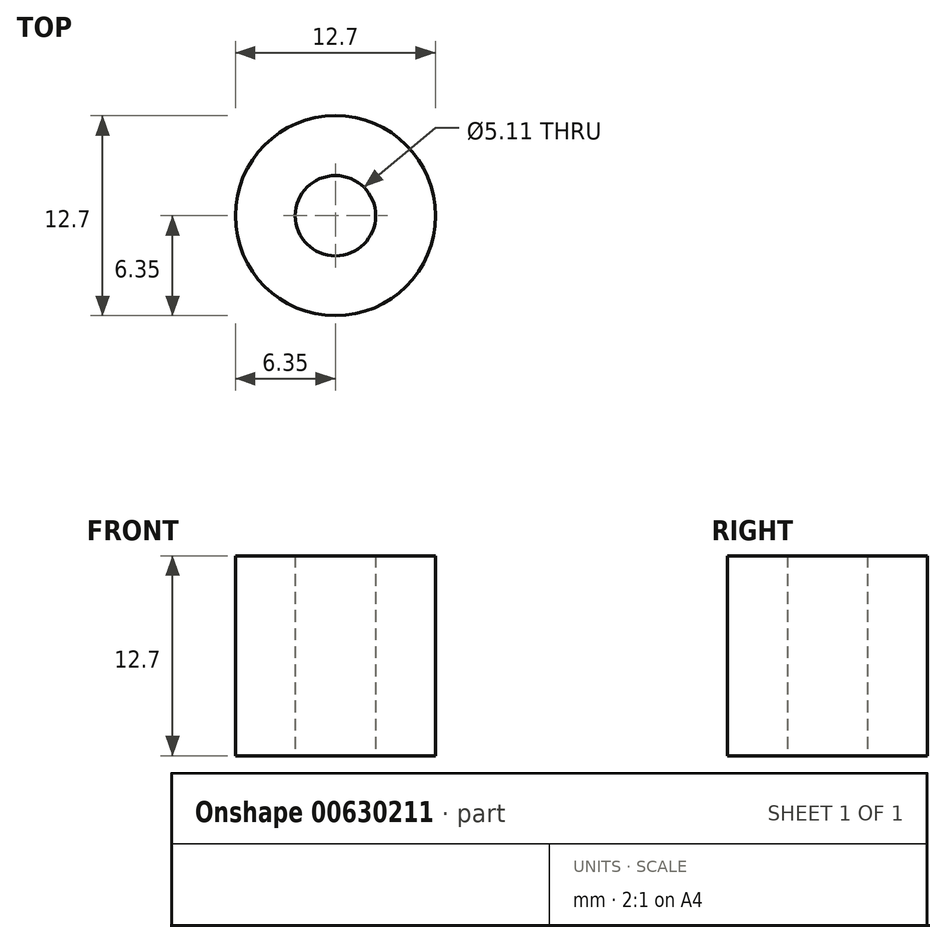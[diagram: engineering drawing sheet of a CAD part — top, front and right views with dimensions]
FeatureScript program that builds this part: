
annotation { "Feature Type Name" : "Feature", "Feature Type Description" : "" }
export const myFeature = defineFeature(function(context is Context, id is Id, definition is map)
    precondition{}
    {
        {
            var Q0;
            Q0=qCreatedBy(makeId("Top.planeOp"),FACE);
            var sketch = newSketch(context, id + "F0", { "sketchPlane" : qUnion([Q0])});
            skCircle(sketch, "E0", {"center": v(0, 0) * mm, "radius": 6.35 * mm});
            skCircle(sketch, "E1", {"center": v(0, 0) * mm, "radius": 2.55 * mm});
            skSolve(sketch);
        }
        {
            var Q0;
            Q0 = qSketchRegion(id + "F0", true);
            extrude(context, id + "F1", {"entities" : qUnion([Q0]), "depth" : 12.7 * mm, "offsetDistance" : 25.4 * mm});
        }
    });
